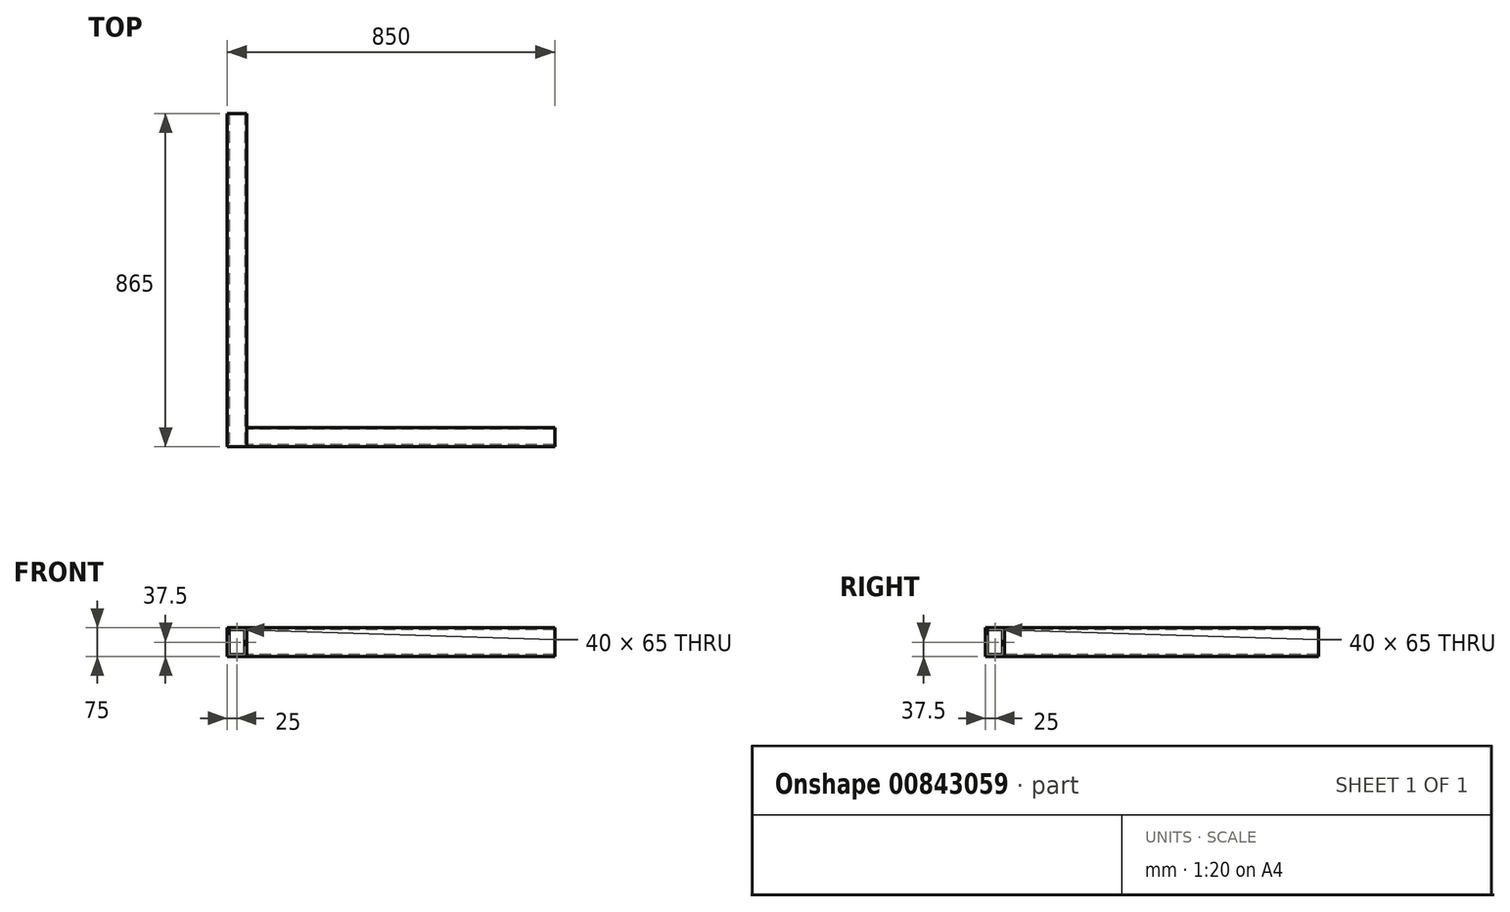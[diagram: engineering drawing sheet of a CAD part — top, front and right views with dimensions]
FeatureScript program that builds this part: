
annotation { "Feature Type Name" : "Feature", "Feature Type Description" : "" }
export const myFeature = defineFeature(function(context is Context, id is Id, definition is map)
    precondition{}
    {
        {
            var Q0;
            Q0=qCreatedBy(makeId("Front.planeOp"),FACE);
            var sketch = newSketch(context, id + "F0", { "sketchPlane" : qUnion([Q0])});
            skLineSegment(sketch, "E0.bottom", {"start": v(0, 0) * mm, "end": v(-50, 0) * mm});
            skLineSegment(sketch, "E0.top", {"start": v(0, 75) * mm, "end": v(-50, 75) * mm});
            skLineSegment(sketch, "E0.left", {"start": v(0, 0) * mm, "end": v(0, 75) * mm});
            skLineSegment(sketch, "E0.right", {"start": v(-50, 0) * mm, "end": v(-50, 75) * mm});
            skLineSegment(sketch, "E1.0", {"start": v(-5, 70) * mm, "end": v(-45, 70) * mm});
            skLineSegment(sketch, "E1.1", {"start": v(-5, 5) * mm, "end": v(-5, 70) * mm});
            skLineSegment(sketch, "E1.2", {"start": v(-5, 5) * mm, "end": v(-45, 5) * mm});
            skLineSegment(sketch, "E1.3", {"start": v(-45, 5) * mm, "end": v(-45, 70) * mm});
            skSolve(sketch);
        }
        {
            var Q0;
            Q0=makeQuery(id+"F0.imprint","IMPRINT",FACE,{"disambiguationData":[TD([[makeQuery(id+"F0.imprint","IMPRINT",EDGE,{"derivedFrom":sQuery(id+"F0.wireOp",EDGE,"E0.bottom")}),-1.0]])]});
            extrude(context, id + "F1", {"entities" : qUnion([Q0]), "oppositeDirection" : true, "depth" : 865 * mm, "offsetDistance" : 25 * mm});
        }
        {
            var Q0;
            Q0=qCreatedBy(makeId("Right.planeOp"),FACE);
            var sketch = newSketch(context, id + "F2", { "sketchPlane" : qUnion([Q0])});
            skLineSegment(sketch, "E2.bottom", {"start": v(0, 0) * mm, "end": v(50, 0) * mm});
            skLineSegment(sketch, "E2.top", {"start": v(0, 75) * mm, "end": v(50, 75) * mm});
            skLineSegment(sketch, "E2.left", {"start": v(0, 0) * mm, "end": v(0, 75) * mm});
            skLineSegment(sketch, "E2.right", {"start": v(50, 0) * mm, "end": v(50, 75) * mm});
            skLineSegment(sketch, "E3.0", {"start": v(5, 5) * mm, "end": v(5, 70) * mm});
            skLineSegment(sketch, "E3.1", {"start": v(5, 5) * mm, "end": v(45, 5) * mm});
            skLineSegment(sketch, "E3.2", {"start": v(45, 5) * mm, "end": v(45, 70) * mm});
            skLineSegment(sketch, "E3.3", {"start": v(5, 70) * mm, "end": v(45, 70) * mm});
            skSolve(sketch);
        }
        {
            var Q0;
            Q0 = qSketchRegion(id + "F2", true);
            extrude(context, id + "F3", {"entities" : qUnion([Q0]), "depth" : 800 * mm, "offsetDistance" : 25 * mm});
        }
    });
